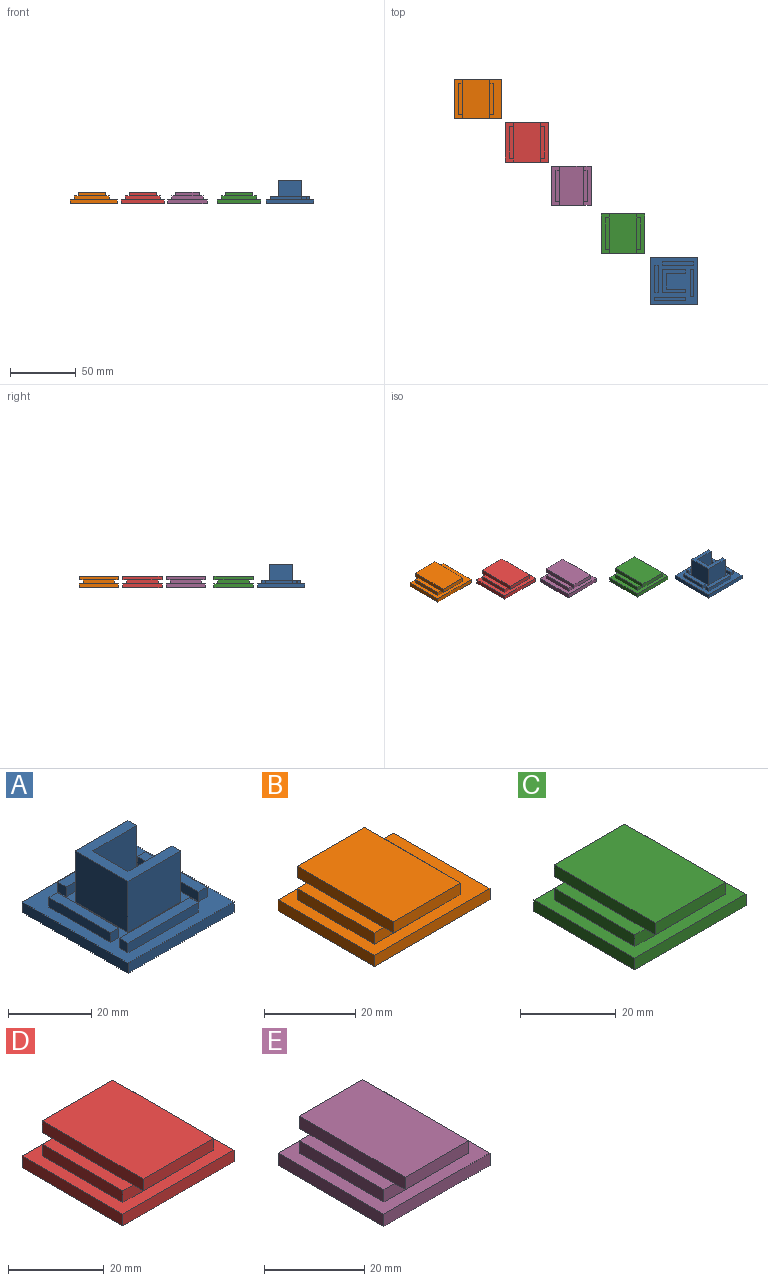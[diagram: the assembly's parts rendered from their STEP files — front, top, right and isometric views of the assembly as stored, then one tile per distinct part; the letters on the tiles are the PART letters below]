
ASSEMBLY  parts=5 mates=4
PART A: 35 faces, bbox 36x36x18 mm
  f0: plane 17.85x17.85mm, normal (0,0,1), area 139.5mm2, adj f1,f20,f21,f22,f31,f32,f33,f34
  f1: plane 17.85x15mm, normal (0,1,0), area 267.7mm2, adj f0,f14,f31,f34
  f2: plane 20.85x2.85mm, normal (0,0,1), area 59.4mm2, adj f3,f4,f25,f30
  f3: plane 2.85x2.85mm, normal (0,-1,0), area 8.1mm2, adj f2,f14,f25,f30
  f4: plane 2.85x2.85mm, normal (0,1,0), area 8.1mm2, adj f2,f14,f25,f30
  f5: plane 23.85x2.85mm, normal (0,0,1), area 68mm2, adj f9,f23,f26,f29
  f6: plane 2.85x2.85mm, normal (-1,0,0), area 8.1mm2, adj f10,f13,f14,f28
  f7: plane 2.85x2.85mm, normal (1,0,0), area 8.1mm2, adj f10,f13,f14,f28
  f8: plane 20.85x2.85mm, normal (-1,0,0), area 59.4mm2, adj f11,f12,f14,f24
  f9: plane 2.85x2.85mm, normal (-1,0,0), area 8.1mm2, adj f5,f14,f23,f29
  f10: plane 23.85x2.85mm, normal (0,0,1), area 68mm2, adj f6,f7,f13,f28
  f11: plane 20.85x2.85mm, normal (0,0,1), area 59.4mm2, adj f8,f12,f24,f27
  f12: plane 2.85x2.85mm, normal (0,-1,0), area 8.1mm2, adj f8,f11,f14,f27
  f13: plane 23.85x2.85mm, normal (0,-1,0), area 68mm2, adj f6,f7,f10,f14
  f14: plane 36x36mm, normal (0,0,1), area 901.7mm2, adj f1,f3,f4,f6,f7,f8,f9,f12
  f15: plane 36x3mm, normal (0,1,0), area 108mm2, adj f14,f16,f18,f19
  f16: plane 36x3mm, normal (1,0,0), area 108mm2, adj f14,f15,f17,f19
  f17: plane 36x3mm, normal (0,-1,0), area 108mm2, adj f14,f16,f18,f19
  f18: plane 36x3mm, normal (-1,0,0), area 108mm2, adj f14,f15,f17,f19
  f19: plane 36x36mm, normal (0,0,-1), area 1296mm2, adj f15,f16,f17,f18
  f20: plane 15x12mm, normal (1,0,0), area 180mm2, adj f0,f14,f21,f22
  f21: plane 15x14.93mm, normal (0,1,0), area 223.9mm2, adj f0,f14,f20,f33
  f22: plane 15x14.93mm, normal (0,-1,0), area 223.9mm2, adj f0,f14,f20,f34
  f23: plane 23.85x2.85mm, normal (0,1,0), area 68mm2, adj f5,f9,f14,f26
  f24: plane 2.85x2.85mm, normal (0,1,0), area 8.1mm2, adj f8,f11,f14,f27
  f25: plane 20.85x2.85mm, normal (1,0,0), area 59.4mm2, adj f2,f3,f4,f14
  f26: plane 2.85x2.85mm, normal (1,0,0), area 8.1mm2, adj f5,f14,f23,f29
  f27: plane 20.85x2.85mm, normal (1,0,0), area 59.4mm2, adj f11,f12,f14,f24
  f28: plane 23.85x2.85mm, normal (0,1,0), area 68mm2, adj f6,f7,f10,f14
  f29: plane 23.85x2.85mm, normal (0,-1,0), area 68mm2, adj f5,f9,f14,f26
  f30: plane 20.85x2.85mm, normal (-1,0,0), area 59.4mm2, adj f2,f3,f4,f14
  f31: plane 17.85x15mm, normal (-1,0,0), area 267.8mm2, adj f0,f1,f14,f32
  f32: plane 17.85x15mm, normal (0,-1,0), area 267.7mm2, adj f0,f14,f31,f33
  f33: plane 15x2.93mm, normal (1,0,0), area 43.9mm2, adj f0,f14,f21,f32
  f34: plane 15x2.93mm, normal (1,0,0), area 43.9mm2, adj f0,f1,f14,f22
PART B: 114 faces, bbox 35.9x29.9x9 mm
  f0: plane 35.85x29.85mm, normal (0,0,1), area 429.8mm2, adj f2,f3,f4,f5,f102,f103,f104,f105
  f1: plane 35.85x29.85mm, normal (0,0,-1), area 1013.1mm2, adj f2,f3,f4,f5,f6,f7,f8,f9
  f2: plane 35.85x3mm, normal (0,1,0), area 107.6mm2, adj f0,f1,f3,f5
  f3: plane 29.85x3mm, normal (-1,0,0), area 89.5mm2, adj f0,f1,f2,f4
  f4: plane 35.85x3mm, normal (0,-1,0), area 107.6mm2, adj f0,f1,f3,f5
  f5: plane 29.85x3mm, normal (1,0,0), area 89.5mm2, adj f0,f1,f2,f4
  f6: extruded ~0.61x0.3mm, area 0.2mm2, adj f1,f7,f18,f19
  f7: extruded ~0.89x0.3mm, area 0.3mm2, adj f1,f6,f8,f19
  f8: extruded ~0.77x0.69mm, area 0.3mm2, adj f1,f7,f9,f19
  f9: plane 0.3x0.04mm, normal (0,1,0), area 0mm2, adj f1,f8,f10,f19
  f10: plane 0.95x0.3mm, normal (-1,0.09,0), area 0.3mm2, adj f1,f9,f11,f19
  f11: plane 0.64x0.3mm, normal (0,1,0), area 0.2mm2, adj f1,f10,f12,f19
  f12: plane 5.14x0.3mm, normal (1,0,0), area 1.5mm2, adj f1,f11,f13,f19
  f13: plane 0.78x0.3mm, normal (0,-1,0), area 0.2mm2, adj f1,f12,f14,f19
  f14: plane 2.76x0.3mm, normal (-1,0,0), area 0.8mm2, adj f1,f13,f15,f19
  f15: extruded ~1.26x0.44mm, area 0.4mm2, adj f1,f14,f16,f19
  f16: extruded ~1.07x0.51mm, area 0.4mm2, adj f1,f15,f17,f19
  f17: extruded ~0.56x0.3mm, area 0.2mm2, adj f1,f16,f18,f19
  f18: plane 0.72x0.3mm, normal (-0.99,-0.15,0), area 0.2mm2, adj f1,f6,f17,f19
  f19: plane 5.24x2.96mm, normal (0,0,-1), area 5.5mm2, adj f6,f7,f8,f9,f10,f11,f12,f13
  f20: plane 3.33x0.3mm, normal (1,0,0), area 1mm2, adj f1,f21,f36,f37
  f21: plane 0.78x0.3mm, normal (0,-1,0), area 0.2mm2, adj f1,f20,f22,f37
  f22: plane 3.35x0.3mm, normal (-1,0,0), area 1mm2, adj f1,f21,f23,f37
  f23: extruded ~1.44x0.47mm, area 0.5mm2, adj f1,f22,f24,f37
  f24: extruded ~1.4x0.45mm, area 0.5mm2, adj f1,f23,f25,f37
  f25: extruded ~0.96x0.3mm, area 0.3mm2, adj f1,f24,f26,f37
  f26: extruded ~0.67x0.59mm, area 0.3mm2, adj f1,f25,f27,f37
  f27: plane 0.3x0.04mm, normal (0,1,0), area 0mm2, adj f1,f26,f28,f37
  f28: plane 0.7x0.3mm, normal (-0.98,0.18,0), area 0.2mm2, adj f1,f27,f29,f37
  f29: plane 0.63x0.3mm, normal (0,1,0), area 0.2mm2, adj f1,f28,f30,f37
  f30: plane 5.14x0.3mm, normal (1,0,0), area 1.5mm2, adj f1,f29,f31,f37
  f31: plane 0.78x0.3mm, normal (0,-1,0), area 0.2mm2, adj f1,f30,f32,f37
  f32: plane 2.7x0.3mm, normal (-1,0,0), area 0.8mm2, adj f1,f31,f33,f37
  f33: extruded ~1.44x0.38mm, area 0.5mm2, adj f1,f32,f34,f37
  f34: extruded ~1.18x0.44mm, area 0.4mm2, adj f1,f33,f35,f37
  f35: extruded ~0.9x0.31mm, area 0.3mm2, adj f1,f34,f36,f37
  f36: extruded ~0.94x0.3mm, area 0.3mm2, adj f1,f20,f35,f37
  f37: plane 5.24x4.3mm, normal (0,0,-1), area 9.6mm2, adj f20,f21,f22,f23,f24,f25,f26,f27
  f38: extruded ~0.99x0.4mm, area 0.3mm2, adj f39,f56,f57,f99
  f39: extruded ~0.94x0.39mm, area 0.3mm2, adj f38,f40,f57,f99
  f40: extruded ~1.13x0.33mm, area 0.4mm2, adj f39,f41,f57,f99
  f41: plane 2.69x0.3mm, normal (0,1,0), area 0.8mm2, adj f40,f56,f57,f99
  f42: extruded ~1.8x0.7mm, area 0.6mm2, adj f1,f43,f55,f57
  f43: extruded ~0.89x0.3mm, area 0.3mm2, adj f1,f42,f44,f57
  f44: extruded ~0.78x0.3mm, area 0.2mm2, adj f1,f43,f45,f57
  f45: plane 0.7x0.3mm, normal (-1,0,0), area 0.2mm2, adj f1,f44,f46,f57
  f46: extruded ~1.64x0.35mm, area 0.5mm2, adj f1,f45,f47,f57
  f47: extruded ~1.22x0.47mm, area 0.4mm2, adj f1,f46,f48,f57
  f48: extruded ~1.37x0.46mm, area 0.4mm2, adj f1,f47,f49,f57
  f49: plane 3.54x0.3mm, normal (0,-1,0), area 1.1mm2, adj f1,f48,f50,f57
  f50: plane 0.49x0.3mm, normal (-1,0,0), area 0.1mm2, adj f1,f49,f51,f57
  f51: extruded ~1.68x0.56mm, area 0.5mm2, adj f1,f50,f52,f57
  f52: extruded ~1.53x0.64mm, area 0.5mm2, adj f1,f51,f53,f57
  f53: extruded ~1.65x0.73mm, area 0.6mm2, adj f1,f52,f54,f57
  f54: extruded ~1.98x0.61mm, area 0.6mm2, adj f1,f53,f55,f57
  f55: extruded ~1.93x0.66mm, area 0.6mm2, adj f1,f42,f54,f57
  f56: extruded ~1.12x0.43mm, area 0.4mm2, adj f38,f41,f57,f99
  f57: plane 5.33x4.35mm, normal (0,0,-1), area 10.6mm2, adj f38,f39,f40,f41,f42,f43,f44,f45
  f58: extruded ~0.99x0.4mm, area 0.3mm2, adj f59,f76,f77,f100
  f59: extruded ~0.94x0.39mm, area 0.3mm2, adj f58,f60,f77,f100
  f60: extruded ~1.13x0.33mm, area 0.4mm2, adj f59,f61,f77,f100
  f61: plane 2.69x0.3mm, normal (0,1,0), area 0.8mm2, adj f60,f76,f77,f100
  f62: extruded ~1.8x0.7mm, area 0.6mm2, adj f1,f63,f75,f77
  f63: extruded ~0.89x0.3mm, area 0.3mm2, adj f1,f62,f64,f77
  f64: extruded ~0.78x0.3mm, area 0.2mm2, adj f1,f63,f65,f77
  f65: plane 0.7x0.3mm, normal (-1,0,0), area 0.2mm2, adj f1,f64,f66,f77
  f66: extruded ~1.64x0.35mm, area 0.5mm2, adj f1,f65,f67,f77
  f67: extruded ~1.22x0.47mm, area 0.4mm2, adj f1,f66,f68,f77
  f68: extruded ~1.37x0.46mm, area 0.4mm2, adj f1,f67,f69,f77
  f69: plane 3.54x0.3mm, normal (0,-1,0), area 1.1mm2, adj f1,f68,f70,f77
  f70: plane 0.49x0.3mm, normal (-1,0,0), area 0.1mm2, adj f1,f69,f71,f77
  f71: extruded ~1.68x0.56mm, area 0.5mm2, adj f1,f70,f72,f77
  f72: extruded ~1.53x0.64mm, area 0.5mm2, adj f1,f71,f73,f77
  f73: extruded ~1.65x0.73mm, area 0.6mm2, adj f1,f72,f74,f77
  f74: extruded ~1.98x0.61mm, area 0.6mm2, adj f1,f73,f75,f77
  f75: extruded ~1.93x0.66mm, area 0.6mm2, adj f1,f62,f74,f77
  f76: extruded ~1.12x0.43mm, area 0.4mm2, adj f58,f61,f77,f100
  f77: plane 5.33x4.35mm, normal (0,0,-1), area 10.6mm2, adj f58,f59,f60,f61,f62,f63,f64,f65
  f78: plane 2.33x0.3mm, normal (0,1,0), area 0.7mm2, adj f1,f79,f97,f98
  f79: plane 0.71x0.3mm, normal (1,0,0), area 0.2mm2, adj f1,f78,f80,f98
  f80: plane 1.53x0.3mm, normal (0,-1,0), area 0.5mm2, adj f1,f79,f81,f98
  f81: plane 2.11x0.3mm, normal (1,0,0), area 0.6mm2, adj f1,f80,f82,f98
  f82: extruded ~1.39x0.3mm, area 0.4mm2, adj f1,f81,f83,f98
  f83: extruded ~1.99x0.72mm, area 0.7mm2, adj f1,f82,f84,f98
  f84: extruded ~2.11x0.68mm, area 0.7mm2, adj f1,f83,f85,f98
  f85: extruded ~2.07x0.7mm, area 0.7mm2, adj f1,f84,f86,f98
  f86: extruded ~1.96x0.75mm, area 0.6mm2, adj f1,f85,f87,f98
  f87: extruded ~1.79x0.39mm, area 0.6mm2, adj f1,f86,f88,f98
  f88: plane 0.7x0.31mm, normal (-0.92,-0.4,0), area 0.2mm2, adj f1,f87,f89,f98
  f89: extruded ~2.05x0.4mm, area 0.6mm2, adj f1,f88,f90,f98
  f90: extruded ~1.89x0.42mm, area 0.6mm2, adj f1,f89,f91,f98
  f91: extruded ~1.24x1.23mm, area 0.5mm2, adj f1,f90,f92,f98
  f92: extruded ~1.88x0.43mm, area 0.6mm2, adj f1,f91,f93,f98
  f93: extruded ~2.6x0.87mm, area 0.8mm2, adj f1,f92,f94,f98
  f94: extruded ~2.43x0.93mm, area 0.8mm2, adj f1,f93,f95,f98
  f95: extruded ~1.31x0.3mm, area 0.4mm2, adj f1,f94,f96,f98
  f96: extruded ~1.11x0.3mm, area 0.3mm2, adj f1,f95,f97,f98
  f97: plane 3.34x0.3mm, normal (-1,0,0), area 1mm2, adj f1,f78,f96,f98
  f98: plane 7.05x5.71mm, normal (0,0,-1), area 14.3mm2, adj f78,f79,f80,f81,f82,f83,f84,f85
  f99: plane 2.69x1.52mm, normal (0,0,-1), area 3.3mm2, adj f38,f39,f40,f41,f56
  f100: plane 2.69x1.52mm, normal (0,0,-1), area 3.3mm2, adj f58,f59,f60,f61,f76
  f101: plane 23.85x3mm, normal (0,0,1), area 71.5mm2, adj f102,f104,f105,f111
  f102: plane 26.85x3mm, normal (0,1,0), area 80.5mm2, adj f0,f101,f103,f105,f106,f113
  f103: plane 23.85x3mm, normal (-1,0,0), area 71.5mm2, adj f0,f102,f104,f106
  f104: plane 26.85x3mm, normal (0,-1,0), area 80.6mm2, adj f0,f101,f103,f105,f106,f107
  f105: plane 23.85x3mm, normal (1,0,0), area 71.5mm2, adj f0,f101,f102,f104
  f106: plane 23.85x3mm, normal (0,0,1), area 71.5mm2, adj f102,f103,f104,f109
  f107: plane 20.85x3mm, normal (0,0,-1), area 62.6mm2, adj f104,f109,f110,f111
  f108: plane 20.85x3mm, normal (0,1,0), area 62.5mm2, adj f109,f111,f112,f113
  f109: plane 29.85x3mm, normal (-1,0,0), area 89.5mm2, adj f106,f107,f108,f110,f112,f113
  f110: plane 20.85x3mm, normal (0,-1,0), area 62.5mm2, adj f107,f109,f111,f112
  f111: plane 29.85x3mm, normal (1,0,0), area 89.5mm2, adj f101,f107,f108,f110,f112,f113
  f112: plane 29.85x20.85mm, normal (0,0,1), area 622.4mm2, adj f108,f109,f110,f111
  f113: plane 20.85x3mm, normal (0,0,-1), area 62.6mm2, adj f102,f108,f109,f111
PART C: 86 faces, bbox 32.9x29.9x9 mm
  f0: plane 20.85x3mm, normal (0,0,-1), area 62.6mm2, adj f1,f2,f4,f10
  f1: plane 20.85x3mm, normal (0,-1,0), area 62.5mm2, adj f0,f2,f4,f6
  f2: plane 29.85x3mm, normal (-1,0,0), area 89.5mm2, adj f0,f1,f3,f5,f6,f12
  f3: plane 20.85x3mm, normal (0,1,0), area 62.5mm2, adj f2,f4,f5,f6
  f4: plane 29.85x3mm, normal (1,0,0), area 89.5mm2, adj f0,f1,f3,f5,f6,f7
  f5: plane 20.85x3mm, normal (0,0,-1), area 62.6mm2, adj f2,f3,f4,f8
  f6: plane 29.85x20.85mm, normal (0,0,1), area 622.4mm2, adj f1,f2,f3,f4
  f7: plane 23.85x3mm, normal (0,0,1), area 71.5mm2, adj f4,f8,f10,f11
  f8: plane 26.85x3mm, normal (0,1,0), area 80.5mm2, adj f5,f7,f9,f11,f12,f18
  f9: plane 23.85x3mm, normal (-1,0,0), area 71.5mm2, adj f8,f10,f12,f18
  f10: plane 26.85x3mm, normal (0,-1,0), area 80.6mm2, adj f0,f7,f9,f11,f12,f18
  f11: plane 23.85x3mm, normal (1,0,0), area 71.5mm2, adj f7,f8,f10,f18
  f12: plane 23.85x3mm, normal (0,0,1), area 71.5mm2, adj f2,f8,f9,f10
  f13: plane 32.85x29.85mm, normal (0,0,-1), area 906.1mm2, adj f14,f15,f16,f17,f27,f28,f29,f30
  f14: plane 32.85x3mm, normal (0,1,0), area 98.6mm2, adj f13,f15,f17,f18
  f15: plane 29.85x3mm, normal (-1,0,0), area 89.5mm2, adj f13,f14,f16,f18
  f16: plane 32.85x3mm, normal (0,-1,0), area 98.6mm2, adj f13,f15,f17,f18
  f17: plane 29.85x3mm, normal (1,0,0), area 89.5mm2, adj f13,f14,f16,f18
  f18: plane 32.85x29.85mm, normal (0,0,1), area 340.2mm2, adj f8,f9,f10,f11,f14,f15,f16,f17
  f19: extruded ~1.32x0.49mm, area 0.4mm2, adj f20,f42,f43,f83
  f20: extruded ~1.21x0.57mm, area 0.4mm2, adj f19,f21,f43,f83
  f21: extruded ~1.7x0.41mm, area 0.5mm2, adj f20,f22,f43,f83
  f22: extruded ~1.71x0.41mm, area 0.5mm2, adj f21,f23,f43,f83
  f23: extruded ~1.2x0.61mm, area 0.4mm2, adj f22,f24,f43,f83
  f24: extruded ~1.32x0.53mm, area 0.4mm2, adj f23,f25,f43,f83
  f25: extruded ~1.78x0.41mm, area 0.6mm2, adj f24,f26,f43,f83
  f26: plane 0.3x0.19mm, normal (1,0,0), area 0.1mm2, adj f25,f42,f43,f83
  f27: plane 0.3x0.05mm, normal (0,-1,0), area 0mm2, adj f13,f28,f41,f43
  f28: plane 0.79x0.3mm, normal (0.99,-0.15,0), area 0.2mm2, adj f13,f27,f29,f43
  f29: plane 0.72x0.3mm, normal (0,-1,0), area 0.2mm2, adj f13,f28,f30,f43
  f30: plane 8.33x0.3mm, normal (-1,0,0), area 2.5mm2, adj f13,f29,f31,f43
  f31: plane 0.89x0.3mm, normal (0,1,0), area 0.3mm2, adj f13,f30,f32,f43
  f32: plane 2.39x0.3mm, normal (1,0,0), area 0.7mm2, adj f13,f31,f33,f43
  f33: plane 0.41x0.3mm, normal (1,-0.05,0), area 0.1mm2, adj f13,f32,f34,f43
  f34: plane 0.42x0.3mm, normal (1,-0.09,0), area 0.1mm2, adj f13,f33,f35,f43
  f35: plane 0.3x0.07mm, normal (0,1,0), area 0mm2, adj f13,f34,f36,f43
  f36: extruded ~1.83x0.87mm, area 0.6mm2, adj f13,f35,f37,f43
  f37: extruded ~1.79x0.8mm, area 0.6mm2, adj f13,f36,f38,f43
  f38: extruded ~2.25x0.64mm, area 0.7mm2, adj f13,f37,f39,f43
  f39: extruded ~2.24x0.64mm, area 0.7mm2, adj f13,f38,f40,f43
  f40: extruded ~1.79x0.79mm, area 0.6mm2, adj f13,f39,f41,f43
  f41: extruded ~1.84x0.89mm, area 0.6mm2, adj f13,f27,f40,f43
  f42: extruded ~1.6x0.41mm, area 0.5mm2, adj f19,f26,f43,f83
  f43: plane 8.43x5.16mm, normal (0,0,-1), area 16.8mm2, adj f19,f20,f21,f22,f23,f24,f25,f26
  f44: extruded ~1.13x0.46mm, area 0.4mm2, adj f45,f62,f63,f84
  f45: extruded ~1.07x0.45mm, area 0.4mm2, adj f44,f46,f63,f84
  f46: extruded ~1.29x0.37mm, area 0.4mm2, adj f45,f47,f63,f84
  f47: plane 3.07x0.3mm, normal (0,1,0), area 0.9mm2, adj f46,f62,f63,f84
  f48: extruded ~2.05x0.79mm, area 0.7mm2, adj f13,f49,f61,f63
  f49: extruded ~1.01x0.3mm, area 0.3mm2, adj f13,f48,f50,f63
  f50: extruded ~0.89x0.3mm, area 0.3mm2, adj f13,f49,f51,f63
  f51: plane 0.79x0.3mm, normal (-1,0,0), area 0.2mm2, adj f13,f50,f52,f63
  f52: extruded ~1.87x0.4mm, area 0.6mm2, adj f13,f51,f53,f63
  f53: extruded ~1.39x0.54mm, area 0.5mm2, adj f13,f52,f54,f63
  f54: extruded ~1.57x0.52mm, area 0.5mm2, adj f13,f53,f55,f63
  f55: plane 4.04x0.3mm, normal (0,-1,0), area 1.2mm2, adj f13,f54,f56,f63
  f56: plane 0.56x0.3mm, normal (-1,0,0), area 0.2mm2, adj f13,f55,f57,f63
  f57: extruded ~1.91x0.64mm, area 0.6mm2, adj f13,f56,f58,f63
  f58: extruded ~1.74x0.73mm, area 0.6mm2, adj f13,f57,f59,f63
  f59: extruded ~1.88x0.83mm, area 0.6mm2, adj f13,f58,f60,f63
  f60: extruded ~2.25x0.7mm, area 0.7mm2, adj f13,f59,f61,f63
  f61: extruded ~2.2x0.75mm, area 0.7mm2, adj f13,f48,f60,f63
  f62: extruded ~1.27x0.5mm, area 0.4mm2, adj f44,f47,f63,f84
  f63: plane 6.08x4.96mm, normal (0,0,-1), area 13.7mm2, adj f44,f45,f46,f47,f48,f49,f50,f51
  f64: plane 1.25x0.3mm, normal (0,1,0), area 0.4mm2, adj f65,f81,f82,f85
  f65: plane 2.99x0.3mm, normal (-1,0,0), area 0.9mm2, adj f64,f66,f82,f85
  f66: plane 1.18x0.3mm, normal (0,-1,0), area 0.4mm2, adj f65,f67,f82,f85
  f67: extruded ~1.47x0.34mm, area 0.5mm2, adj f66,f68,f82,f85
  f68: extruded ~1.12x0.46mm, area 0.4mm2, adj f67,f69,f82,f85
  f69: extruded ~1.15x0.45mm, area 0.4mm2, adj f68,f81,f82,f85
  f70: plane 3.25x0.3mm, normal (-1,0,0), area 1mm2, adj f13,f71,f80,f82
  f71: plane 1.63x0.3mm, normal (0,-1,0), area 0.5mm2, adj f13,f70,f72,f82
  f72: plane 3.25x1.89mm, normal (0.86,-0.5,0), area 1.1mm2, adj f13,f71,f73,f82
  f73: plane 1.08x0.3mm, normal (0,-1,0), area 0.3mm2, adj f13,f72,f74,f82
  f74: plane 3.51x2.12mm, normal (-0.86,0.52,0), area 1.2mm2, adj f13,f73,f75,f82
  f75: extruded ~2.1x1.57mm, area 0.8mm2, adj f13,f74,f76,f82
  f76: extruded ~1.66x0.69mm, area 0.6mm2, adj f13,f75,f77,f82
  f77: extruded ~2.13x0.55mm, area 0.7mm2, adj f13,f76,f78,f82
  f78: plane 2.15x0.3mm, normal (0,1,0), area 0.6mm2, adj f13,f77,f79,f82
  f79: plane 7.82x0.3mm, normal (1,0,0), area 2.3mm2, adj f13,f78,f80,f82
  f80: plane 0.91x0.3mm, normal (0,-1,0), area 0.3mm2, adj f13,f70,f79,f82
  f81: extruded ~1.41x0.38mm, area 0.4mm2, adj f64,f69,f82,f85
  f82: plane 7.82x5.51mm, normal (0,0,-1), area 18.3mm2, adj f64,f65,f66,f67,f68,f69,f70,f71
  f83: plane 4.59x3.35mm, normal (0,0,-1), area 12.9mm2, adj f19,f20,f21,f22,f23,f24,f25,f26
  f84: plane 3.07x1.73mm, normal (0,0,-1), area 4.3mm2, adj f44,f45,f46,f47,f62
  f85: plane 3.11x2.99mm, normal (0,0,-1), area 8.4mm2, adj f64,f65,f66,f67,f68,f69,f81
PART D: 91 faces, bbox 32.9x29.9x9 mm
  f0: plane 32.85x29.85mm, normal (0,0,1), area 340.2mm2, adj f2,f3,f4,f5,f79,f80,f81,f82
  f1: plane 32.85x29.85mm, normal (0,0,-1), area 941mm2, adj f2,f3,f4,f5,f6,f7,f8,f9
  f2: plane 32.85x3mm, normal (0,1,0), area 98.6mm2, adj f0,f1,f3,f5
  f3: plane 29.85x3mm, normal (-1,0,0), area 89.5mm2, adj f0,f1,f2,f4
  f4: plane 32.85x3mm, normal (0,-1,0), area 98.6mm2, adj f0,f1,f3,f5
  f5: plane 29.85x3mm, normal (1,0,0), area 89.5mm2, adj f0,f1,f2,f4
  f6: plane 0.64x0.3mm, normal (0,-1,0), area 0.2mm2, adj f1,f7,f9,f10
  f7: plane 6.01x0.3mm, normal (-1,0,0), area 1.8mm2, adj f1,f6,f8,f10
  f8: plane 0.64x0.3mm, normal (0,1,0), area 0.2mm2, adj f1,f7,f9,f10
  f9: plane 6.01x0.3mm, normal (1,0,0), area 1.8mm2, adj f1,f6,f8,f10
  f10: plane 6.01x0.64mm, normal (0,0,-1), area 3.9mm2, adj f6,f7,f8,f9
  f11: plane 2.75x0.3mm, normal (-1,0,0), area 0.8mm2, adj f1,f12,f27,f28
  f12: plane 0.65x0.3mm, normal (0,1,0), area 0.2mm2, adj f1,f11,f13,f28
  f13: plane 2.77x0.3mm, normal (1,0,0), area 0.8mm2, adj f1,f12,f14,f28
  f14: extruded ~1.17x0.38mm, area 0.4mm2, adj f1,f13,f15,f28
  f15: extruded ~1.16x0.37mm, area 0.4mm2, adj f1,f14,f16,f28
  f16: extruded ~0.8x0.3mm, area 0.2mm2, adj f1,f15,f17,f28
  f17: extruded ~0.55x0.48mm, area 0.2mm2, adj f1,f16,f18,f28
  f18: plane 0.3x0.03mm, normal (0,-1,0), area 0mm2, adj f1,f17,f19,f28
  f19: plane 0.57x0.3mm, normal (0.99,-0.16,0), area 0.2mm2, adj f1,f18,f20,f28
  f20: plane 0.53x0.3mm, normal (0,-1,0), area 0.2mm2, adj f1,f19,f21,f28
  f21: plane 4.23x0.3mm, normal (-1,0,0), area 1.3mm2, adj f1,f20,f22,f28
  f22: plane 0.64x0.3mm, normal (0,1,0), area 0.2mm2, adj f1,f21,f23,f28
  f23: plane 2.23x0.3mm, normal (1,0,0), area 0.7mm2, adj f1,f22,f24,f28
  f24: extruded ~1.19x0.31mm, area 0.4mm2, adj f1,f23,f25,f28
  f25: extruded ~0.97x0.36mm, area 0.3mm2, adj f1,f24,f26,f28
  f26: extruded ~0.74x0.3mm, area 0.2mm2, adj f1,f25,f27,f28
  f27: extruded ~0.77x0.3mm, area 0.2mm2, adj f1,f11,f26,f28
  f28: plane 4.31x3.54mm, normal (0,0,-1), area 6.5mm2, adj f11,f12,f13,f14,f15,f16,f17,f18
  f29: extruded ~0.81x0.33mm, area 0.3mm2, adj f30,f47,f48,f76
  f30: extruded ~0.77x0.32mm, area 0.3mm2, adj f29,f31,f48,f76
  f31: extruded ~0.93x0.3mm, area 0.3mm2, adj f30,f32,f48,f76
  f32: plane 2.21x0.3mm, normal (0,1,0), area 0.7mm2, adj f31,f47,f48,f76
  f33: extruded ~1.48x0.57mm, area 0.5mm2, adj f1,f34,f46,f48
  f34: extruded ~0.73x0.3mm, area 0.2mm2, adj f1,f33,f35,f48
  f35: extruded ~0.64x0.3mm, area 0.2mm2, adj f1,f34,f36,f48
  f36: plane 0.57x0.3mm, normal (-1,0,0), area 0.2mm2, adj f1,f35,f37,f48
  f37: extruded ~1.35x0.3mm, area 0.4mm2, adj f1,f36,f38,f48
  f38: extruded ~1.01x0.39mm, area 0.3mm2, adj f1,f37,f39,f48
  f39: extruded ~1.13x0.38mm, area 0.4mm2, adj f1,f38,f40,f48
  f40: plane 2.92x0.3mm, normal (0,-1,0), area 0.9mm2, adj f1,f39,f41,f48
  f41: plane 0.41x0.3mm, normal (-1,0,0), area 0.1mm2, adj f1,f40,f42,f48
  f42: extruded ~1.38x0.46mm, area 0.4mm2, adj f1,f41,f43,f48
  f43: extruded ~1.26x0.52mm, area 0.4mm2, adj f1,f42,f44,f48
  f44: extruded ~1.36x0.6mm, area 0.5mm2, adj f1,f43,f45,f48
  f45: extruded ~1.63x0.5mm, area 0.5mm2, adj f1,f44,f46,f48
  f46: extruded ~1.59x0.54mm, area 0.5mm2, adj f1,f33,f45,f48
  f47: extruded ~0.92x0.36mm, area 0.3mm2, adj f29,f32,f48,f76
  f48: plane 4.39x3.58mm, normal (0,0,-1), area 7.2mm2, adj f29,f30,f31,f32,f33,f34,f35,f36
  f49: plane 2.11x0.3mm, normal (-1,0,0), area 0.6mm2, adj f50,f73,f74,f77
  f50: plane 1.13x0.3mm, normal (0,-1,0), area 0.3mm2, adj f49,f51,f74,f77
  f51: extruded ~1.08x0.3mm, area 0.3mm2, adj f50,f52,f74,f77
  f52: extruded ~0.77x0.35mm, area 0.3mm2, adj f51,f53,f74,f77
  f53: extruded ~0.83x0.35mm, area 0.3mm2, adj f52,f54,f74,f77
  f54: extruded ~1.03x0.3mm, area 0.3mm2, adj f53,f73,f74,f77
  f55: plane 1.08x0.3mm, normal (0,1,0), area 0.3mm2, adj f56,f71,f74,f75
  f56: plane 1.85x0.3mm, normal (-1,0,0), area 0.6mm2, adj f55,f57,f74,f75
  f57: plane 0.97x0.3mm, normal (0,-1,0), area 0.3mm2, adj f56,f58,f74,f75
  f58: extruded ~1.08x0.3mm, area 0.3mm2, adj f57,f59,f74,f75
  f59: extruded ~0.69x0.34mm, area 0.2mm2, adj f58,f60,f74,f75
  f60: extruded ~0.74x0.31mm, area 0.2mm2, adj f59,f71,f74,f75
  f61: plane 1.6x0.3mm, normal (0,1,0), area 0.5mm2, adj f1,f62,f72,f74
  f62: plane 5.65x0.3mm, normal (1,0,0), area 1.7mm2, adj f1,f61,f63,f74
  f63: plane 1.97x0.3mm, normal (0,-1,0), area 0.6mm2, adj f1,f62,f64,f74
  f64: extruded ~1.43x0.43mm, area 0.5mm2, adj f1,f63,f65,f74
  f65: extruded ~1.18x0.51mm, area 0.4mm2, adj f1,f64,f66,f74
  f66: extruded ~1.35x1.29mm, area 0.6mm2, adj f1,f65,f67,f74
  f67: plane 0.3x0.04mm, normal (-1,0,0), area 0mm2, adj f1,f66,f68,f74
  f68: extruded ~0.82x0.42mm, area 0.3mm2, adj f1,f67,f69,f74
  f69: extruded ~0.83x0.3mm, area 0.3mm2, adj f1,f68,f70,f74
  f70: extruded ~1.06x0.5mm, area 0.4mm2, adj f1,f69,f72,f74
  f71: extruded ~1x0.3mm, area 0.3mm2, adj f55,f60,f74,f75
  f72: extruded ~1.63x0.34mm, area 0.5mm2, adj f1,f61,f70,f74
  f73: plane 1.18x0.3mm, normal (0,1,0), area 0.4mm2, adj f49,f54,f74,f77
  f74: plane 5.65x3.91mm, normal (0,0,-1), area 10.9mm2, adj f49,f50,f51,f52,f53,f54,f55,f56
  f75: plane 2.39x1.85mm, normal (0,0,-1), area 4mm2, adj f55,f56,f57,f58,f59,f60,f71
  f76: plane 2.21x1.25mm, normal (0,0,-1), area 2.2mm2, adj f29,f30,f31,f32,f47
  f77: plane 2.55x2.11mm, normal (0,0,-1), area 4.9mm2, adj f49,f50,f51,f52,f53,f54,f73
  f78: plane 23.85x3mm, normal (0,0,1), area 71.5mm2, adj f79,f80,f81,f86
  f79: plane 26.85x3mm, normal (0,1,0), area 80.5mm2, adj f0,f78,f80,f82,f83,f84
  f80: plane 23.85x3mm, normal (-1,0,0), area 71.5mm2, adj f0,f78,f79,f81
  f81: plane 26.85x3mm, normal (0,-1,0), area 80.6mm2, adj f0,f78,f80,f82,f83,f89
  f82: plane 23.85x3mm, normal (1,0,0), area 71.5mm2, adj f0,f79,f81,f83
  f83: plane 23.85x3mm, normal (0,0,1), area 71.5mm2, adj f79,f81,f82,f88
  f84: plane 20.85x3mm, normal (0,0,-1), area 62.6mm2, adj f79,f86,f87,f88
  f85: plane 20.85x3mm, normal (0,-1,0), area 62.5mm2, adj f86,f88,f89,f90
  f86: plane 29.85x3mm, normal (-1,0,0), area 89.5mm2, adj f78,f84,f85,f87,f89,f90
  f87: plane 20.85x3mm, normal (0,1,0), area 62.5mm2, adj f84,f86,f88,f90
  f88: plane 29.85x3mm, normal (1,0,0), area 89.5mm2, adj f83,f84,f85,f87,f89,f90
  f89: plane 20.85x3mm, normal (0,0,-1), area 62.6mm2, adj f81,f85,f86,f88
  f90: plane 29.85x20.85mm, normal (0,0,1), area 622.4mm2, adj f85,f86,f87,f88
PART E: 103 faces, bbox 29.9x29.9x9 mm
  f0: plane 17.85x3mm, normal (0,0,-1), area 53.6mm2, adj f1,f2,f4,f10
  f1: plane 17.85x3mm, normal (0,-1,0), area 53.5mm2, adj f0,f2,f4,f6
  f2: plane 29.85x3mm, normal (-1,0,0), area 89.5mm2, adj f0,f1,f3,f5,f6,f12
  f3: plane 17.85x3mm, normal (0,1,0), area 53.5mm2, adj f2,f4,f5,f6
  f4: plane 29.85x3mm, normal (1,0,0), area 89.5mm2, adj f0,f1,f3,f5,f6,f7
  f5: plane 17.85x3mm, normal (0,0,-1), area 53.6mm2, adj f2,f3,f4,f8
  f6: plane 29.85x17.85mm, normal (0,0,1), area 532.8mm2, adj f1,f2,f3,f4
  f7: plane 23.85x3mm, normal (0,0,1), area 71.6mm2, adj f4,f8,f10,f11
  f8: plane 23.85x3mm, normal (0,1,0), area 71.5mm2, adj f5,f7,f9,f11,f12,f18
  f9: plane 23.85x3mm, normal (-1,0,0), area 71.5mm2, adj f8,f10,f12,f18
  f10: plane 23.85x3mm, normal (0,-1,0), area 71.5mm2, adj f0,f7,f9,f11,f12,f18
  f11: plane 23.85x3mm, normal (1,0,0), area 71.5mm2, adj f7,f8,f10,f18
  f12: plane 23.85x3mm, normal (0,0,1), area 71.5mm2, adj f2,f8,f9,f10
  f13: plane 29.85x29.85mm, normal (0,0,-1), area 859.8mm2, adj f14,f15,f16,f17,f23,f24,f25,f26
  f14: plane 29.85x3mm, normal (0,1,0), area 89.5mm2, adj f13,f15,f17,f18
  f15: plane 29.85x3mm, normal (-1,0,0), area 89.5mm2, adj f13,f14,f16,f18
  f16: plane 29.85x3mm, normal (0,-1,0), area 89.5mm2, adj f13,f15,f17,f18
  f17: plane 29.85x3mm, normal (1,0,0), area 89.5mm2, adj f13,f14,f16,f18
  f18: plane 29.85x29.85mm, normal (0,0,1), area 322.2mm2, adj f8,f9,f10,f11,f14,f15,f16,f17
  f19: extruded ~0.66x0.3mm, area 0.2mm2, adj f20,f37,f38,f101
  f20: extruded ~0.63x0.3mm, area 0.2mm2, adj f19,f21,f38,f101
  f21: extruded ~0.76x0.3mm, area 0.2mm2, adj f20,f22,f38,f101
  f22: plane 1.81x0.3mm, normal (0,1,0), area 0.5mm2, adj f21,f37,f38,f101
  f23: extruded ~1.21x0.47mm, area 0.4mm2, adj f13,f24,f36,f38
  f24: extruded ~0.6x0.3mm, area 0.2mm2, adj f13,f23,f25,f38
  f25: extruded ~0.52x0.3mm, area 0.2mm2, adj f13,f24,f26,f38
  f26: plane 0.47x0.3mm, normal (-1,0,0), area 0.1mm2, adj f13,f25,f27,f38
  f27: extruded ~1.1x0.3mm, area 0.3mm2, adj f13,f26,f28,f38
  f28: extruded ~0.82x0.32mm, area 0.3mm2, adj f13,f27,f29,f38
  f29: extruded ~0.92x0.31mm, area 0.3mm2, adj f13,f28,f30,f38
  f30: plane 2.38x0.3mm, normal (0,-1,0), area 0.7mm2, adj f13,f29,f31,f38
  f31: plane 0.33x0.3mm, normal (-1,0,0), area 0.1mm2, adj f13,f30,f32,f38
  f32: extruded ~1.13x0.38mm, area 0.4mm2, adj f13,f31,f33,f38
  f33: extruded ~1.03x0.43mm, area 0.3mm2, adj f13,f32,f34,f38
  f34: extruded ~1.11x0.49mm, area 0.4mm2, adj f13,f33,f35,f38
  f35: extruded ~1.33x0.41mm, area 0.4mm2, adj f13,f34,f36,f38
  f36: extruded ~1.3x0.44mm, area 0.4mm2, adj f13,f23,f35,f38
  f37: extruded ~0.75x0.3mm, area 0.2mm2, adj f19,f22,f38,f101
  f38: plane 3.58x2.92mm, normal (0,0,-1), area 4.8mm2, adj f19,f20,f21,f22,f23,f24,f25,f26
  f39: plane 2.03x0.63mm, normal (0.95,-0.3,0), area 0.6mm2, adj f13,f40,f61,f62
  f40: plane 0.62x0.3mm, normal (0,-1,0), area 0.2mm2, adj f13,f39,f41,f62
  f41: plane 3.46x0.95mm, normal (-0.96,-0.27,0), area 1.1mm2, adj f13,f40,f42,f62
  f42: plane 0.54x0.3mm, normal (0,1,0), area 0.2mm2, adj f13,f41,f43,f62
  f43: extruded ~2.54x0.66mm, area 0.8mm2, adj f13,f42,f44,f62
  f44: extruded ~0.35x0.3mm, area 0.1mm2, adj f13,f43,f45,f62
  f45: plane 0.3x0.03mm, normal (0,1,0), area 0mm2, adj f13,f44,f46,f62
  f46: extruded ~0.91x0.3mm, area 0.3mm2, adj f13,f45,f47,f62
  f47: plane 1.98x0.62mm, normal (-0.95,0.3,0), area 0.6mm2, adj f13,f46,f48,f62
  f48: plane 0.57x0.3mm, normal (0,1,0), area 0.2mm2, adj f13,f47,f49,f62
  f49: plane 1.98x0.63mm, normal (0.95,0.3,0), area 0.6mm2, adj f13,f48,f50,f62
  f50: extruded ~0.45x0.3mm, area 0.1mm2, adj f13,f49,f51,f62
  f51: extruded ~0.47x0.3mm, area 0.1mm2, adj f13,f50,f52,f62
  f52: plane 0.3x0.03mm, normal (0,1,0), area 0mm2, adj f13,f51,f53,f62
  f53: extruded ~0.92x0.3mm, area 0.3mm2, adj f13,f52,f54,f62
  f54: extruded ~1.98x0.51mm, area 0.6mm2, adj f13,f53,f55,f62
  f55: plane 0.55x0.3mm, normal (0,1,0), area 0.2mm2, adj f13,f54,f56,f62
  f56: plane 3.46x0.94mm, normal (0.96,-0.26,0), area 1.1mm2, adj f13,f55,f57,f62
  f57: plane 0.61x0.3mm, normal (0,-1,0), area 0.2mm2, adj f13,f56,f58,f62
  f58: plane 2.02x0.65mm, normal (-0.95,-0.31,0), area 0.6mm2, adj f13,f57,f59,f62
  f59: extruded ~0.85x0.3mm, area 0.3mm2, adj f13,f58,f60,f62
  f60: plane 0.3x0.03mm, normal (0,-1,0), area 0mm2, adj f13,f59,f61,f62
  f61: extruded ~0.85x0.3mm, area 0.3mm2, adj f13,f39,f60,f62
  f62: plane 4.88x3.46mm, normal (0,0,-1), area 6.6mm2, adj f39,f40,f41,f42,f43,f44,f45,f46
  f63: plane 0.52x0.3mm, normal (0,-1,0), area 0.2mm2, adj f13,f64,f66,f67
  f64: plane 4.91x0.3mm, normal (-1,0,0), area 1.5mm2, adj f13,f63,f65,f67
  f65: plane 0.52x0.3mm, normal (0,1,0), area 0.2mm2, adj f13,f64,f66,f67
  f66: plane 4.91x0.3mm, normal (1,0,0), area 1.5mm2, adj f13,f63,f65,f67
  f67: plane 4.91x0.52mm, normal (0,0,-1), area 2.6mm2, adj f63,f64,f65,f66
  f68: plane 0.52x0.3mm, normal (0,-1,0), area 0.2mm2, adj f13,f69,f71,f72
  f69: plane 4.91x0.3mm, normal (-1,0,0), area 1.5mm2, adj f13,f68,f70,f72
  f70: plane 0.52x0.3mm, normal (0,1,0), area 0.2mm2, adj f13,f69,f71,f72
  f71: plane 4.91x0.3mm, normal (1,0,0), area 1.5mm2, adj f13,f68,f70,f72
  f72: plane 4.91x0.52mm, normal (0,0,-1), area 2.6mm2, adj f68,f69,f70,f71
  f73: extruded ~1.01x0.3mm, area 0.3mm2, adj f74,f89,f90,f102
  f74: extruded ~1.01x0.3mm, area 0.3mm2, adj f73,f75,f90,f102
  f75: extruded ~0.78x0.34mm, area 0.3mm2, adj f74,f76,f90,f102
  f76: extruded ~0.79x0.34mm, area 0.3mm2, adj f75,f77,f90,f102
  f77: extruded ~1x0.3mm, area 0.3mm2, adj f76,f78,f90,f102
  f78: extruded ~1.01x0.3mm, area 0.3mm2, adj f77,f79,f90,f102
  f79: extruded ~0.78x0.35mm, area 0.3mm2, adj f78,f89,f90,f102
  f80: extruded ~1.32x0.43mm, area 0.4mm2, adj f13,f81,f88,f90
  f81: extruded ~1.31x0.43mm, area 0.4mm2, adj f13,f80,f82,f90
  f82: extruded ~1.15x0.48mm, area 0.4mm2, adj f13,f81,f83,f90
  f83: extruded ~1.17x0.47mm, area 0.4mm2, adj f13,f82,f84,f90
  f84: extruded ~1.32x0.42mm, area 0.4mm2, adj f13,f83,f85,f90
  f85: extruded ~0.95x0.3mm, area 0.3mm2, adj f13,f84,f86,f90
  f86: extruded ~0.62x0.56mm, area 0.3mm2, adj f13,f85,f87,f90
  f87: extruded ~0.82x0.3mm, area 0.3mm2, adj f13,f86,f88,f90
  f88: extruded ~1.18x0.47mm, area 0.4mm2, adj f13,f80,f87,f90
  f89: extruded ~0.78x0.35mm, area 0.3mm2, adj f73,f79,f90,f102
  f90: plane 3.58x3.18mm, normal (0,0,-1), area 4.6mm2, adj f73,f74,f75,f76,f77,f78,f79,f80
  f91: plane 2.31x1.23mm, normal (0.88,0.47,0), area 0.8mm2, adj f13,f92,f99,f100
  f92: plane 2.31x1.22mm, normal (-0.88,0.47,0), area 0.8mm2, adj f13,f91,f93,f100
  f93: plane 0.59x0.3mm, normal (0,1,0), area 0.2mm2, adj f13,f92,f94,f100
  f94: plane 2.85x1.54mm, normal (0.88,-0.47,0), area 1mm2, adj f13,f93,f95,f100
  f95: plane 1.76x0.3mm, normal (1,0,0), area 0.5mm2, adj f13,f94,f96,f100
  f96: plane 0.54x0.3mm, normal (0,-1,0), area 0.2mm2, adj f13,f95,f97,f100
  f97: plane 1.79x0.3mm, normal (-1,0,0), area 0.5mm2, adj f13,f96,f98,f100
  f98: plane 2.82x1.54mm, normal (-0.88,-0.48,0), area 1mm2, adj f13,f97,f99,f100
  f99: plane 0.58x0.3mm, normal (0,1,0), area 0.2mm2, adj f13,f91,f98,f100
  f100: plane 4.61x3.62mm, normal (0,0,-1), area 4mm2, adj f91,f92,f93,f94,f95,f96,f97,f98
  f101: plane 1.81x1.02mm, normal (0,0,-1), area 1.5mm2, adj f19,f20,f21,f22,f37
  f102: plane 2.7x2.09mm, normal (0,0,-1), area 4.7mm2, adj f73,f74,f75,f76,f77,f78,f79,f89
PLACE A t=(94.6,-157.3,0)mm
PLACE B t=(-16.7,160.27,0)mm
PLACE C rot(axis=(1,0,0),0deg) t=(95.27,107.14,0)mm
PLACE D t=(22.04,222.82,0)mm
PLACE E rot(axis=(1,0,0),0deg) t=(57.47,236.57,0)mm
MATE planar C.f13 <-> B.f1  axis (0,0,-1) through (141.59,-120.27,0)mm
MATE planar C.f13 <-> A.f19  axis (0,0,-1) through (141.59,-120.27,0)mm
MATE planar C.f13 <-> D.f1  axis (0,0,-1) through (141.59,-120.27,0)mm
MATE planar C.f13 <-> E.f13  axis (0,0,-1) through (141.59,-120.27,0)mm
